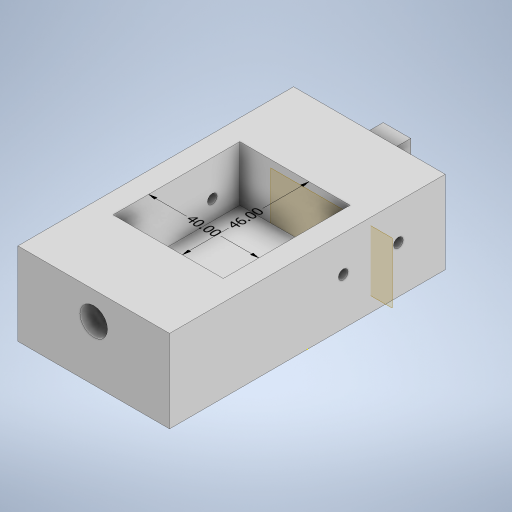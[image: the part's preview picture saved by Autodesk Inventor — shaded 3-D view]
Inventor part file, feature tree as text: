
AUTODESK INVENTOR PART (.ipt)
format: ipt  version: 2023 (Build 270158000, 158)  size: 300,544 bytes
history: native  units: mm
features: sketch x8, extrude x6, other x4, plane x3, hole x1
ambient origin geometry x8: Origin, YZ Plane, XZ Plane, XY Plane, X Axis, Y Axis, Z Axis, Center Point
bodies: Body1 (feature_tree)
feature tree (22):
  other  "Sólido1"
  other  "Anotaciones"
  extrude  "Extrusión1"  Depth=100.0mm
  extrude  "Extrusión2"  Depth=10.0mm
  extrude  "Extrusión3"  Depth=5.0mm
  extrude  "Extrusión4"  Depth=10.0mm TaperAngle=0.0deg
  plane  "Plano de trabajo1"
  extrude  "Extrusión5"  Depth=10.0mm
  plane  "Plano de trabajo2"
  extrude  "Extrusión6"  Depth=40.0mm
  sketch  "Boceto7"  dims[d15=46.0mm d16=20.0mm d17=0.0mm]
  plane  "Plano de trabajo4"
  hole  "Agujero1"  [1 undecoded]
  sketch  "Boceto1"  dims[d0=55.0mm d1=100.0mm]
  sketch  "Boceto2"  dims[d2=30.0mm d3=0.0mm d4=10.0mm]
  sketch  "Boceto3"  dims[d5=20.0mm d6=5.0mm]
  sketch  "Boceto4"  dims[d7=22.5mm d8=10.0mm d9=0.0mm]
  sketch  "Boceto5"  dims[d10=10.0mm d11=10.0mm]
  sketch  "Boceto6"  dims[d12=15.0mm d13=0.0mm d14=40.0mm]
  sketch  "Boceto8"  dims[d24=22.5mm d25=2.5mm d26=2.5mm d27=8.0mm d28=0.0mm d29=3.0mm d30=3.0mm d31=8.0mm d32=0.0mm d33=0.0mm d34=10.0mm d35=30.0mm d36=5.0mm d37=5.0mm d38=5.0mm d39=5.0mm d40=10.0mm d41=8.0mm d42=3.5mm d43=6.0mm d44=4.0mm d45=2.0mm d46=90.0deg d47=8.0mm d48=20.594885mm d18=5.462798mm d19=4.90751mm d20=46.0mm d21=4.68859mm d22=6.124374mm d23=40.0mm]
  other  "Cota lineal 1"
  other  "Cota lineal 2"
note: 1 required parameter value undecoded (feature->parameter linkage not recoverable at this tier; creation-order binding heuristic only, values carry confidence <= 0.55)
